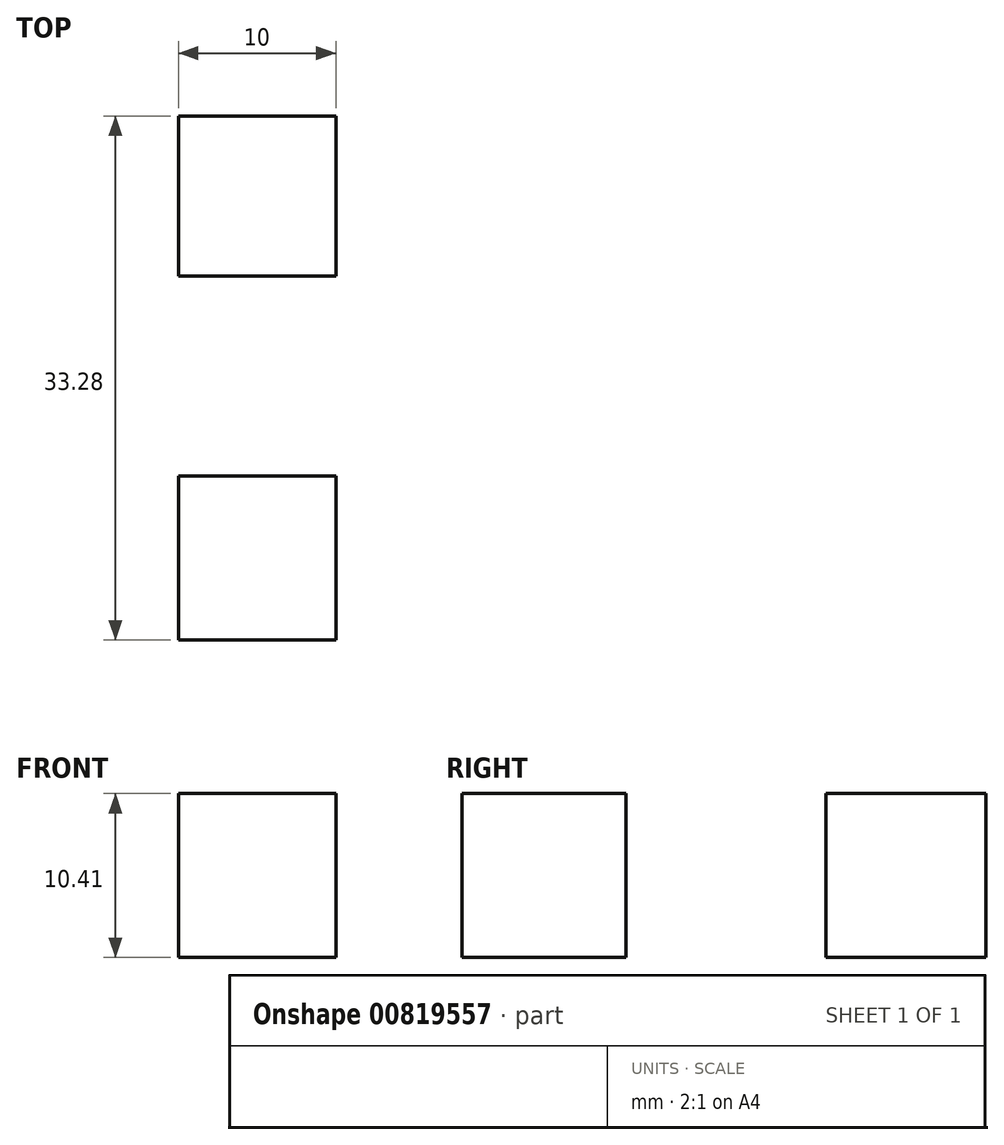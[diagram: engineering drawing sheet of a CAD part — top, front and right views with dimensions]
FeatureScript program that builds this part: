
annotation { "Feature Type Name" : "Feature", "Feature Type Description" : "" }
export const myFeature = defineFeature(function(context is Context, id is Id, definition is map)
    precondition{}
    {
        {
            var Q0;
            Q0=qCreatedBy(makeId("Right.planeOp"),FACE);
            var sketch = newSketch(context, id + "F0", { "sketchPlane" : qUnion([Q0])});
            skLineSegment(sketch, "E0", {"start": v(-53.98, 39.5) * mm, "end": v(-53.98, 29.09) * mm});
            skLineSegment(sketch, "E1", {"start": v(-53.98, 39.5) * mm, "end": v(-43.57, 39.5) * mm});
            skLineSegment(sketch, "E2", {"start": v(-43.57, 39.5) * mm, "end": v(-43.57, 29.09) * mm});
            skLineSegment(sketch, "E3", {"start": v(-53.98, 29.09) * mm, "end": v(-43.57, 29.09) * mm});
            skLineSegment(sketch, "E4", {"start": v(-30.86, 39.5) * mm, "end": v(-30.86, 29.09) * mm});
            skLineSegment(sketch, "E5", {"start": v(-30.86, 39.5) * mm, "end": v(-20.7, 39.5) * mm});
            skLineSegment(sketch, "E6", {"start": v(-20.7, 39.5) * mm, "end": v(-20.7, 29.09) * mm});
            skLineSegment(sketch, "E7", {"start": v(-30.86, 29.09) * mm, "end": v(-20.7, 29.09) * mm});
            skLineSegment(sketch, "E8", {"start": v(-8, 39.5) * mm, "end": v(-8, 29.09) * mm});
            skLineSegment(sketch, "E9", {"start": v(-8, 29.09) * mm, "end": v(-8, 39.5) * mm});
            skLineSegment(sketch, "E10", {"start": v(-8, 39.5) * mm, "end": v(2.16, 39.5) * mm});
            skLineSegment(sketch, "E11", {"start": v(2.16, 29.09) * mm, "end": v(-8, 29.09) * mm});
            skLineSegment(sketch, "E12", {"start": v(2.16, 29.09) * mm, "end": v(2.16, 39.5) * mm});
            skSolve(sketch);
        }
        {
            var Q0;
            Q0=makeQuery(id+"F0.imprint","IMPRINT",FACE,{"disambiguationData":[TD([[makeQuery(id+"F0.imprint","IMPRINT",EDGE,{"derivedFrom":sQuery(id+"F0.wireOp",EDGE,"E4")}),1.0]])]});
            var Q1;
            Q1=makeQuery(id+"F0.imprint","IMPRINT",FACE,{"disambiguationData":[TD([[makeQuery(id+"F0.imprint","IMPRINT",EDGE,{"derivedFrom":sQuery(id+"F0.wireOp",EDGE,"E9")}),-1.0]])]});
            var Q2;
            Q2=makeQuery(id+"F0.imprint","IMPRINT",FACE,{"disambiguationData":[TD([[makeQuery(id+"F0.imprint","IMPRINT",EDGE,{"derivedFrom":sQuery(id+"F0.wireOp",EDGE,"E0")}),1.0]])]});
            extrude(context, id + "F1", {"entities" : qUnion([Q0, Q1, Q2]), "depth" : 10 * mm, "offsetDistance" : 25 * mm});
        }
    });
